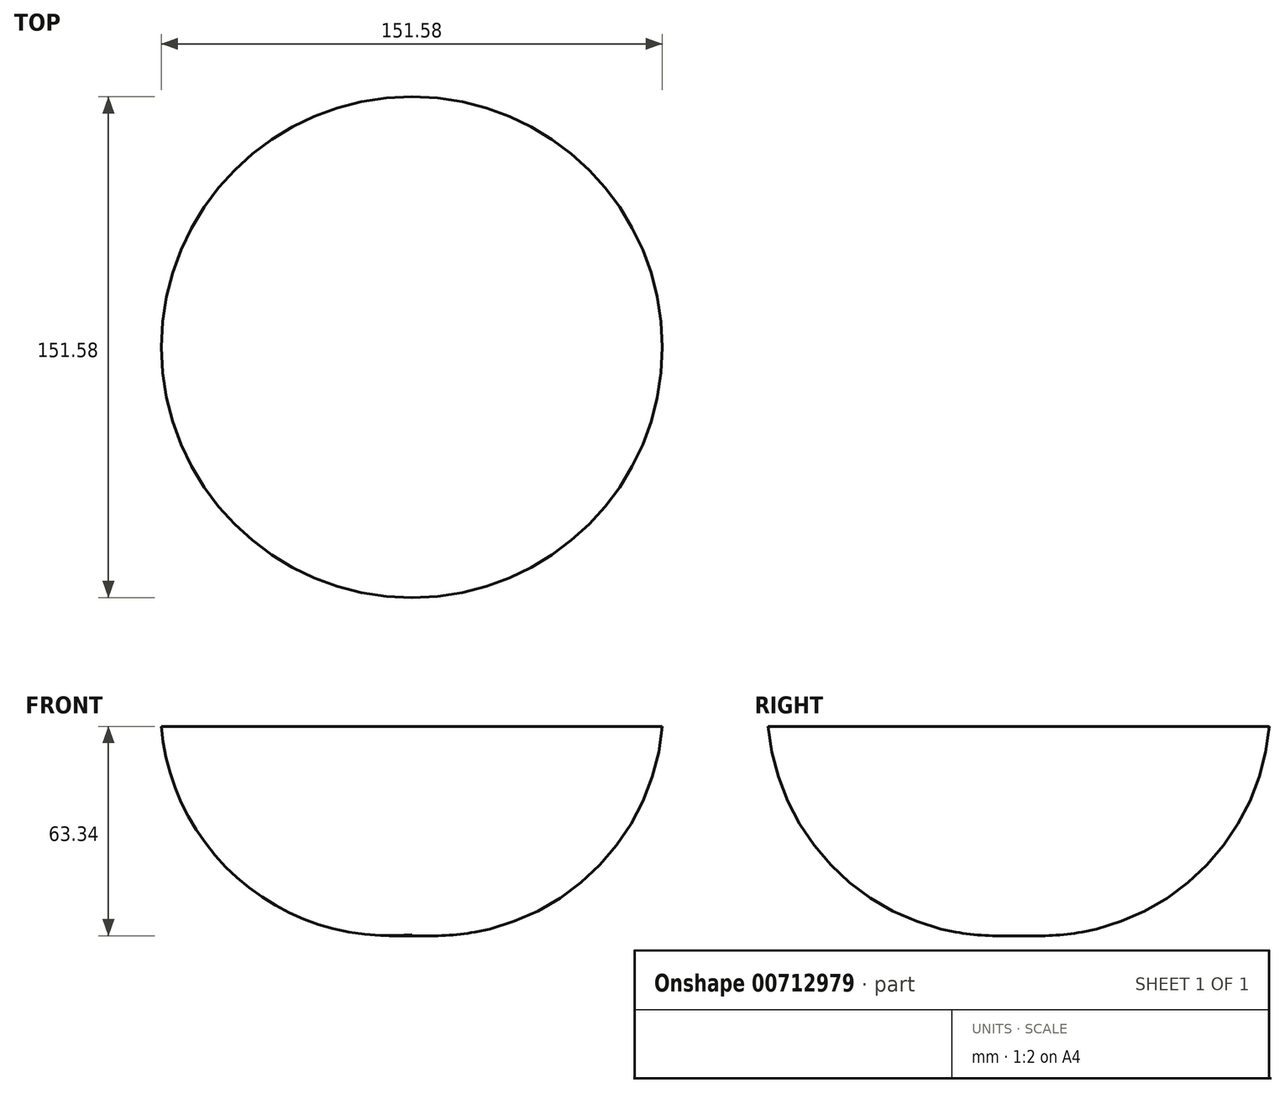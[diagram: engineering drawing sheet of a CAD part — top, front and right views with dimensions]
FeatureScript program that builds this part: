
annotation { "Feature Type Name" : "Feature", "Feature Type Description" : "" }
export const myFeature = defineFeature(function(context is Context, id is Id, definition is map)
    precondition{}
    {
        {
            var Q0;
            Q0=qCreatedBy(makeId("Front.planeOp"),FACE);
            var sketch = newSketch(context, id + "F0", { "sketchPlane" : qUnion([Q0])});
            skLineSegment(sketch, "E0", {"start": v(0, 0) * mm, "end": v(0, 74.72) * mm});
            skLineSegment(sketch, "E1", {"start": v(0, 0) * mm, "end": v(75.79, 0) * mm});
            skArc(sketch, "E2", {"start": v(75.79, 0) * mm, "mid": v(55.42, 55.14) * mm, "end": v(0, 74.72) * mm});
            skSolve(sketch);
        }
        {
            var Q0;
            Q0=makeQuery(id+"F0.imprint","IMPRINT",FACE,{"disambiguationData":[TD([[makeQuery(id+"F0.imprint","IMPRINT",EDGE,{"derivedFrom":sQuery(id+"F0.wireOp",EDGE,"E0")}),-1.0]])]});
            var Q1;
            Q1=sQuery(id+"F0.wireOp",EDGE,"E0");
            revolve(context, id + "F1", {"surfaceOperationType" : NewSurfaceOperationType.NEW, "entities" : qUnion([Q0]), "axis" : qUnion([Q1]), "revolveType" : RevolveType.FULL});
        }
    });
